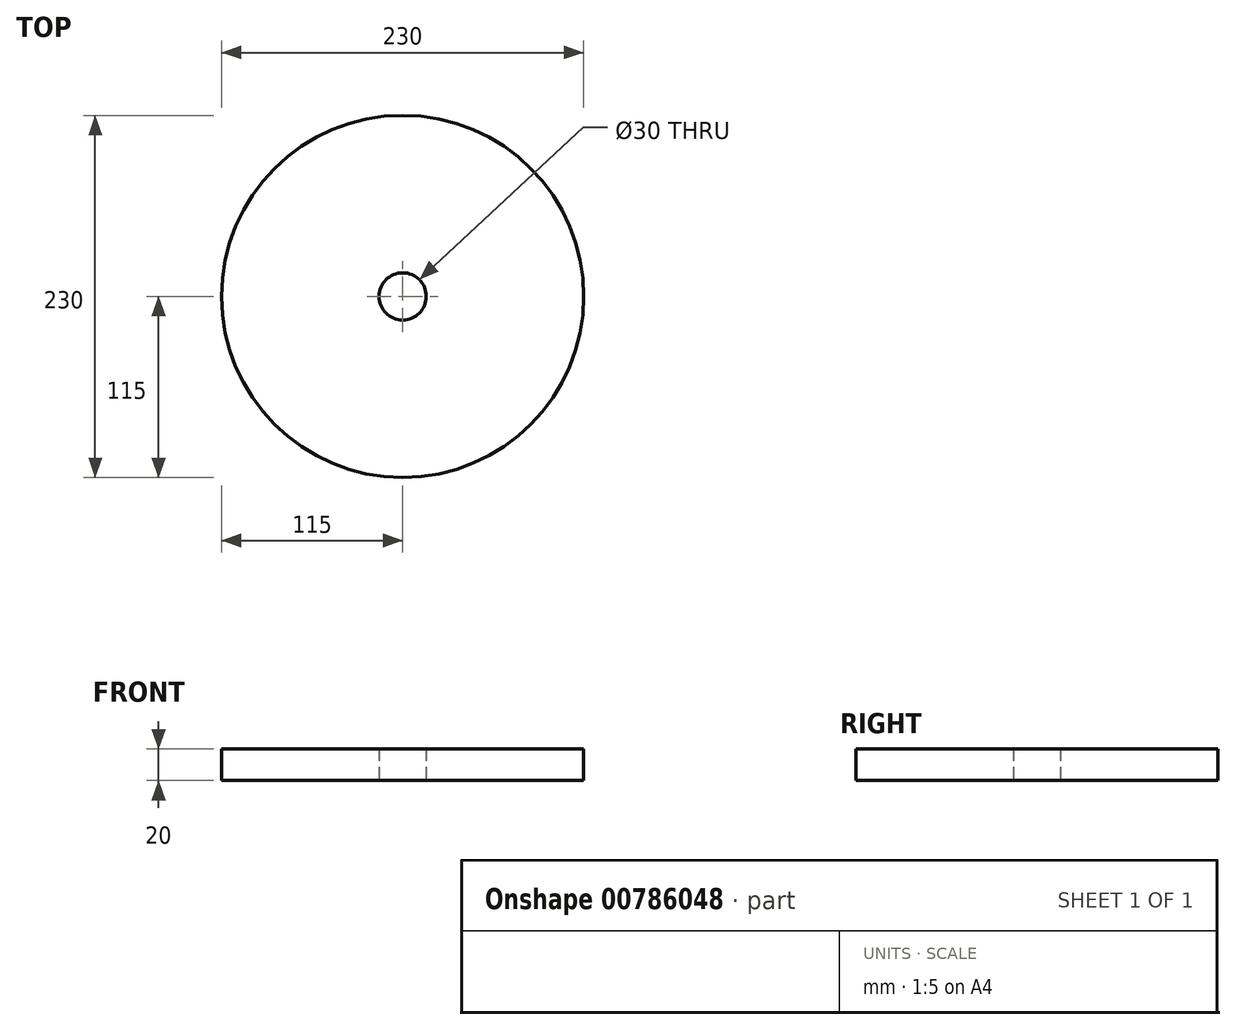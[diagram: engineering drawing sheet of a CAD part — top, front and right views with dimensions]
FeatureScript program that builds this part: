
annotation { "Feature Type Name" : "Feature", "Feature Type Description" : "" }
export const myFeature = defineFeature(function(context is Context, id is Id, definition is map)
    precondition{}
    {
        {
            var Q0;
            Q0=qCreatedBy(makeId("Top.planeOp"),FACE);
            var sketch = newSketch(context, id + "F0", { "sketchPlane" : qUnion([Q0])});
            skCircle(sketch, "E0", {"center": v(0, 0) * mm, "radius": 115 * mm});
            skCircle(sketch, "E1", {"center": v(0, 0) * mm, "radius": 15 * mm});
            skSolve(sketch);
        }
        {
            var Q0;
            Q0=qSketchRegion(id+"F0",true);
            extrude(context, id + "F1", {"entities" : qUnion([Q0]), "depth" : 20 * mm});
        }
    });
